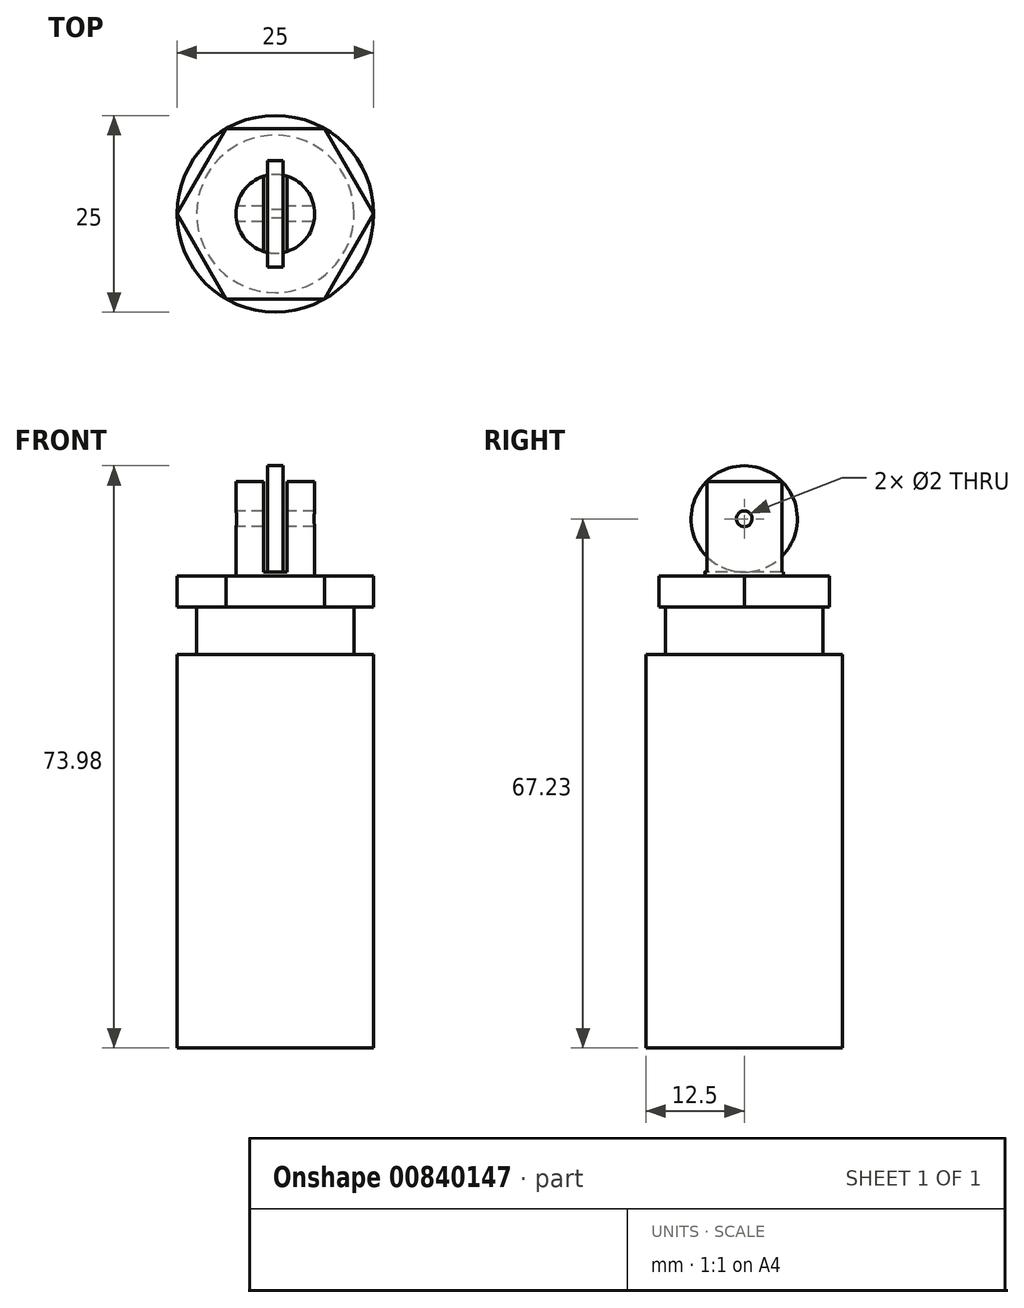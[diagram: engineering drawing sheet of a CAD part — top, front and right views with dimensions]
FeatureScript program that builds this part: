
annotation { "Feature Type Name" : "Feature", "Feature Type Description" : "" }
export const myFeature = defineFeature(function(context is Context, id is Id, definition is map)
    precondition{}
    {
        {
            var Q0;
            Q0=qCreatedBy(makeId("Top.planeOp"),FACE);
            var sketch = newSketch(context, id + "F0", { "sketchPlane" : qUnion([Q0])});
            skCircle(sketch, "E0", {"center": v(0, 0) * mm, "radius": 12.5 * mm});
            skSolve(sketch);
        }
        {
            var Q0;
            Q0=makeQuery(id+"F0.imprint","IMPRINT",FACE,{"disambiguationData":[TD([[makeQuery(id+"F0.imprint","IMPRINT",EDGE,{"derivedFrom":sQuery(id+"F0.wireOp",EDGE,"E0")}),1.0]])]});
            extrude(context, id + "F1", {"entities" : qUnion([Q0]), "oppositeDirection" : true, "depth" : 50 * mm, "offsetDistance" : 25 * mm});
        }
        {
            var Q0;
            Q0=qCreatedBy(makeId("Top.planeOp"),FACE);
            var sketch = newSketch(context, id + "F2", { "sketchPlane" : qUnion([Q0])});
            skCircle(sketch, "E1", {"center": v(0, 0) * mm, "radius": 10 * mm});
            skSolve(sketch);
        }
        {
            var Q0;
            Q0=makeQuery(id+"F2.imprint","IMPRINT",FACE,{"disambiguationData":[TD([[makeQuery(id+"F2.imprint","IMPRINT",EDGE,{"derivedFrom":sQuery(id+"F2.wireOp",EDGE,"E1")}),1.0]])]});
            extrude(context, id + "F3", {"entities" : qUnion([Q0]), "operationType" : NewBodyOperationType.ADD, "depth" : 10 * mm, "offsetDistance" : 25 * mm});
        }
        {
            var Q0;
            Q0=makeQuery(id+"F3.opExtrude","CAP_FACE",FACE,{"disambiguationData":[OSD([sQuery(id+"F2.wireOp",EDGE,"E1")])],"isStart":false});
            var sketch = newSketch(context, id + "F4", { "sketchPlane" : qUnion([Q0])});
            skCircle(sketch, "E2", {"center": v(0, 0) * mm, "radius": 5 * mm});
            skSolve(sketch);
        }
        {
            var Q0;
            Q0 = qSketchRegion(id + "F4", true);
            extrude(context, id + "F5", {"entities" : qUnion([Q0]), "operationType" : NewBodyOperationType.ADD, "depth" : 12 * mm, "offsetDistance" : 25 * mm});
        }
        {
            var Q0;
            Q0=qCreatedBy(makeId("Front.planeOp"),FACE);
            var sketch = newSketch(context, id + "F6", { "sketchPlane" : qUnion([Q0])});
            skLineSegment(sketch, "E3.bottom", {"start": v(1.5, 22) * mm, "end": v(-1.5, 22) * mm});
            skLineSegment(sketch, "E3.top", {"start": v(1.5, 10.5) * mm, "end": v(-1.5, 10.5) * mm});
            skLineSegment(sketch, "E3.left", {"start": v(1.5, 22) * mm, "end": v(1.5, 10.5) * mm});
            skLineSegment(sketch, "E3.right", {"start": v(-1.5, 22) * mm, "end": v(-1.5, 10.5) * mm});
            skLineSegment(sketch, "E4", {"start": v(0, 0) * mm, "end": v(0, 32.13) * mm, "construction": true});
            skSolve(sketch);
        }
        {
            var Q0;
            Q0 = qSketchRegion(id + "F6", true);
            extrude(context, id + "F7", {"entities" : qUnion([Q0]), "operationType" : NewBodyOperationType.REMOVE, "endBound" : BoundingType.THROUGH_ALL, "oppositeDirection" : true, "depth" : 25 * mm, "offsetDistance" : 25 * mm, "hasSecondDirection" : true, "secondDirectionBound" : SecondDirectionBoundingType.THROUGH_ALL, "secondDirectionOppositeDirection" : false, "secondDirectionDepth" : 25 * mm});
        }
        {
            var Q0;
            Q0=makeQuery(id+"F7.boolean.opBoolean","COPY",FACE,{"derivedFrom":makeQuery(id+"F7.opExtrude","SWEPT_FACE",FACE,{"disambiguationData":[OSD([sQuery(id+"F6.wireOp",EDGE,"E3.right")])]})});
            var sketch = newSketch(context, id + "F8", { "sketchPlane" : qUnion([Q0])});
            skLineSegment(sketch, "E5", {"start": v(-4.77, 22) * mm, "end": v(4.77, 12.46) * mm, "construction": true});
            skLineSegment(sketch, "E6", {"start": v(4.77, 22) * mm, "end": v(-4.77, 12.46) * mm, "construction": true});
            skCircle(sketch, "E7", {"center": v(0, 17.23) * mm, "radius": 1 * mm});
            skSolve(sketch);
        }
        {
            var Q0;
            Q0 = qSketchRegion(id + "F8", true);
            extrude(context, id + "F9", {"entities" : qUnion([Q0]), "operationType" : NewBodyOperationType.REMOVE, "endBound" : BoundingType.THROUGH_ALL, "depth" : 25 * mm, "offsetDistance" : 25 * mm, "hasSecondDirection" : true, "secondDirectionBound" : SecondDirectionBoundingType.THROUGH_ALL, "secondDirectionOppositeDirection" : true, "secondDirectionDepth" : 25 * mm});
        }
        {
            var Q0;
            Q0=makeQuery(id+"F3.opExtrude","CAP_FACE",FACE,{"disambiguationData":[OSD([sQuery(id+"F2.wireOp",EDGE,"E1")])],"isStart":false});
            var sketch = newSketch(context, id + "F10", { "sketchPlane" : qUnion([Q0])});
            skCircle(sketch, "E8.cCircle", {"center": v(0, 0) * mm, "radius": 12.5 * mm, "construction": true});
            skLineSegment(sketch, "E8.0", {"start": v(12.5, 0) * mm, "end": v(6.25, -10.83) * mm});
            skLineSegment(sketch, "E8.1", {"start": v(6.25, -10.83) * mm, "end": v(-6.25, -10.83) * mm});
            skLineSegment(sketch, "E8.2", {"start": v(-6.25, -10.83) * mm, "end": v(-12.5, 0) * mm});
            skLineSegment(sketch, "E8.3", {"start": v(-12.5, 0) * mm, "end": v(-6.25, 10.83) * mm});
            skLineSegment(sketch, "E8.4", {"start": v(-6.25, 10.83) * mm, "end": v(6.25, 10.83) * mm});
            skLineSegment(sketch, "E8.5", {"start": v(6.25, 10.83) * mm, "end": v(12.5, 0) * mm});
            skSolve(sketch);
        }
        {
            var Q0;
            Q0 = qSketchRegion(id + "F10", true);
            extrude(context, id + "F11", {"entities" : qUnion([Q0]), "operationType" : NewBodyOperationType.ADD, "oppositeDirection" : true, "depth" : 4 * mm, "offsetDistance" : 25 * mm});
        }
        {
            var Q0;
            Q0=qCreatedBy(makeId("Right.planeOp"),FACE);
            var sketch = newSketch(context, id + "F12", { "sketchPlane" : qUnion([Q0])});
            skCircle(sketch, "E9", {"center": v(0, 17.23) * mm, "radius": 6.75 * mm});
            skSolve(sketch);
        }
        {
            var Q0;
            Q0 = qSketchRegion(id + "F12", true);
            extrude(context, id + "F13", {"entities" : qUnion([Q0]), "operationType" : NewBodyOperationType.ADD, "depth" : 1 * mm, "offsetDistance" : 25 * mm, "hasSecondDirection" : true, "secondDirectionOppositeDirection" : true, "secondDirectionDepth" : 1 * mm});
        }
    });
